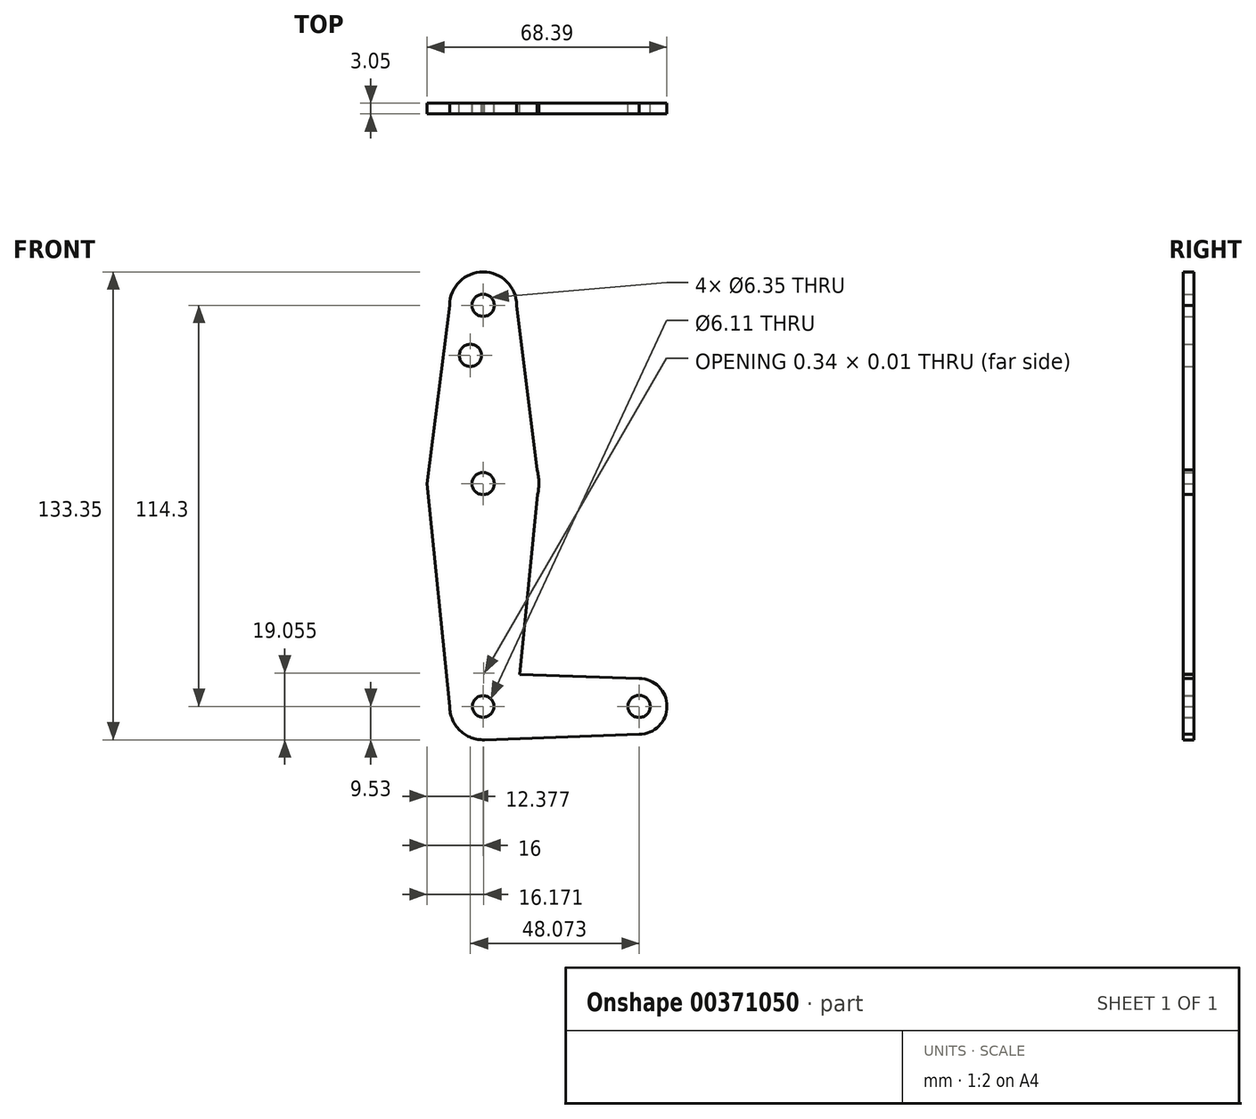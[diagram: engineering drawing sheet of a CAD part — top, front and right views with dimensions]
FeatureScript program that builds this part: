
annotation { "Feature Type Name" : "Feature", "Feature Type Description" : "" }
export const myFeature = defineFeature(function(context is Context, id is Id, definition is map)
    precondition{}
    {
        {
            var Q0;
            Q0=qCreatedBy(makeId("Front.planeOp"),FACE);
            var sketch = newSketch(context, id + "F0", { "sketchPlane" : qUnion([Q0])});
            skCircle(sketch, "E0", {"center": v(0, 0) * mm, "radius": 15.88 * mm});
            skCircle(sketch, "E1", {"center": v(0, -63.5) * mm, "radius": 9.53 * mm});
            skLineSegment(sketch, "E2", {"start": v(0, -63.5) * mm, "end": v(44.45, -63.5) * mm});
            skCircle(sketch, "E3", {"center": v(44.45, -63.5) * mm, "radius": 7.94 * mm});
            skCircle(sketch, "E4", {"center": v(0, 50.8) * mm, "radius": 9.53 * mm});
            skLineSegment(sketch, "E5", {"start": v(0, 50.8) * mm, "end": v(0, -63.5) * mm});
            skLineSegment(sketch, "E6", {"start": v(15.88, 0) * mm, "end": v(9.52, 50.8) * mm});
            skLineSegment(sketch, "E7", {"start": v(-9.52, 50.8) * mm, "end": v(-16, 0) * mm});
            skLineSegment(sketch, "E8", {"start": v(-9.53, -63.5) * mm, "end": v(-16, 0) * mm});
            skPoint(sketch, "E9", {"position": v(9.53, -63.5) * mm});
            skLineSegment(sketch, "E10", {"start": v(44.45, -55.56) * mm, "end": v(0, -53.97) * mm});
            skLineSegment(sketch, "E11", {"start": v(44.45, -71.44) * mm, "end": v(0, -73.03) * mm});
            skPoint(sketch, "E12", {"position": v(10.44, -54.34) * mm});
            skLineSegment(sketch, "E13", {"start": v(15.88, 0) * mm, "end": v(10.44, -54.34) * mm});
            skCircle(sketch, "E14", {"center": v(0, 50.8) * mm, "radius": 3.18 * mm});
            skCircle(sketch, "E15", {"center": v(0, 0) * mm, "radius": 3.18 * mm});
            skCircle(sketch, "E16", {"center": v(0, -63.5) * mm, "radius": 3.06 * mm});
            skCircle(sketch, "E17", {"center": v(44.45, -63.5) * mm, "radius": 3.18 * mm});
            skCircle(sketch, "E18", {"center": v(-3.62, 36.53) * mm, "radius": 3.18 * mm});
            skSolve(sketch);
        }
        {
            var Q0;
            Q0 = qSketchRegion(id + "F0", true);
            var Q1;
            {var subQ1=sQuery(id+"F0.wireOp",EDGE,"E1");var subQ5=makeQuery(id+"F0.imprint","INTERSECT",VERTEX,{"derivedFrom":[subQ1,sQuery(id+"F0.wireOp",EDGE,"E10")]});Q1=makeQuery(id+"F0.imprint","IMPRINT",FACE,{"disambiguationData":[TD([[makeQuery(id+"F0.imprint","IMPRINT",EDGE,{"disambiguationData":[TD([[subQ5,1.0]])],"derivedFrom":subQ1}),1.0]])]});}
            extrude(context, id + "F1", {"entities" : qUnion([Q0, Q1]), "depth" : 3.05 * mm});
        }
    });
